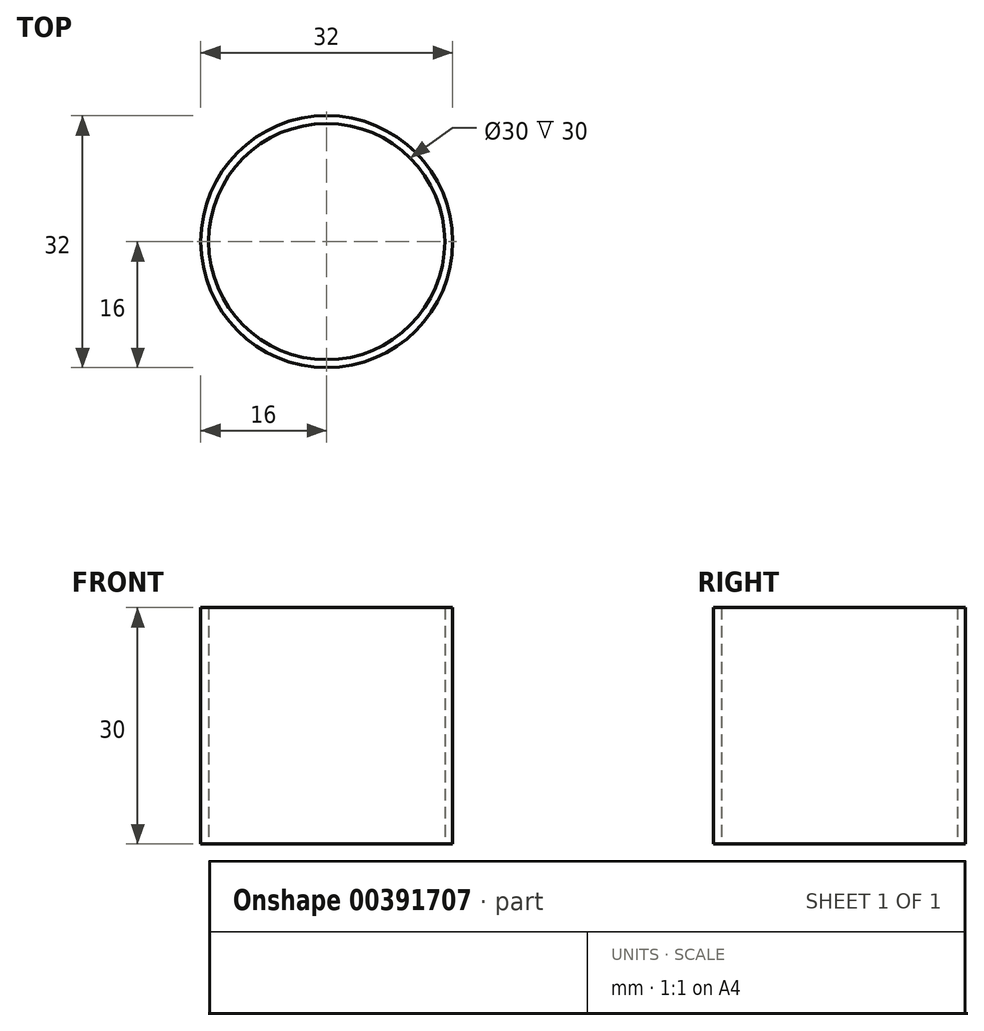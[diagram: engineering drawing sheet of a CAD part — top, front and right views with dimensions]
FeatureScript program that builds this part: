
annotation { "Feature Type Name" : "Feature", "Feature Type Description" : "" }
export const myFeature = defineFeature(function(context is Context, id is Id, definition is map)
    precondition{}
    {
        {
            var Q0;
            Q0=qCreatedBy(makeId("Top.planeOp"),FACE);
            var sketch = newSketch(context, id + "F0", { "sketchPlane" : qUnion([Q0])});
            skCircle(sketch, "E0", {"center": v(0, 0) * mm, "radius": 16 * mm});
            skCircle(sketch, "E1", {"center": v(0, 0) * mm, "radius": 15 * mm});
            skSolve(sketch);
        }
        {
            var Q0;
            Q0=makeQuery(id+"F0.imprint","IMPRINT",FACE,{"disambiguationData":[TD([[makeQuery(id+"F0.imprint","IMPRINT",EDGE,{"derivedFrom":sQuery(id+"F0.wireOp",EDGE,"E0")}),1.0]])]});
            extrude(context, id + "F1", {"entities" : qUnion([Q0]), "depth" : 30 * mm});
        }
    });
